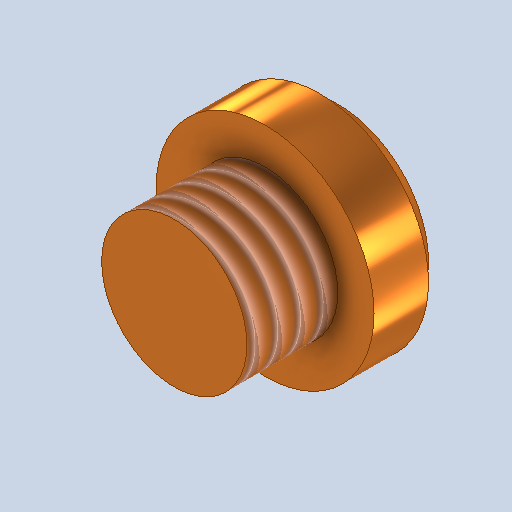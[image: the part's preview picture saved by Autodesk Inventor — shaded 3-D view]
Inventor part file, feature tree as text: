
AUTODESK INVENTOR PART (.ipt)
format: ipt  version: 2025.1 (Build 291241000, 241)  size: 265,728 bytes
history: native  units: mm
features: revolve x1, chamfer x1, thread x1, sketch x1
ambient origin geometry x8: Origin, YZ Plane, XZ Plane, XY Plane, X Axis, Y Axis, Z Axis, Center Point
bodies: Volumenkörper1 (feature_tree)
feature tree (4):
  revolve  "Umdrehung1"
  chamfer  "Fasen1"  Distance=12.0mm
  thread  "Gewinde1"  [1 undecoded]
  sketch  "Skizze1"  dims[d0=8.0mm d1=12.0mm d2=5.0mm d3=4.0mm d4=90.0deg d5=1.0mm d6=2.0mm d7=45.0deg d8=5.0mm d9=0.0mm]
note: 1 required parameter value undecoded (feature->parameter linkage not recoverable at this tier; creation-order binding heuristic only, values carry confidence <= 0.55)
